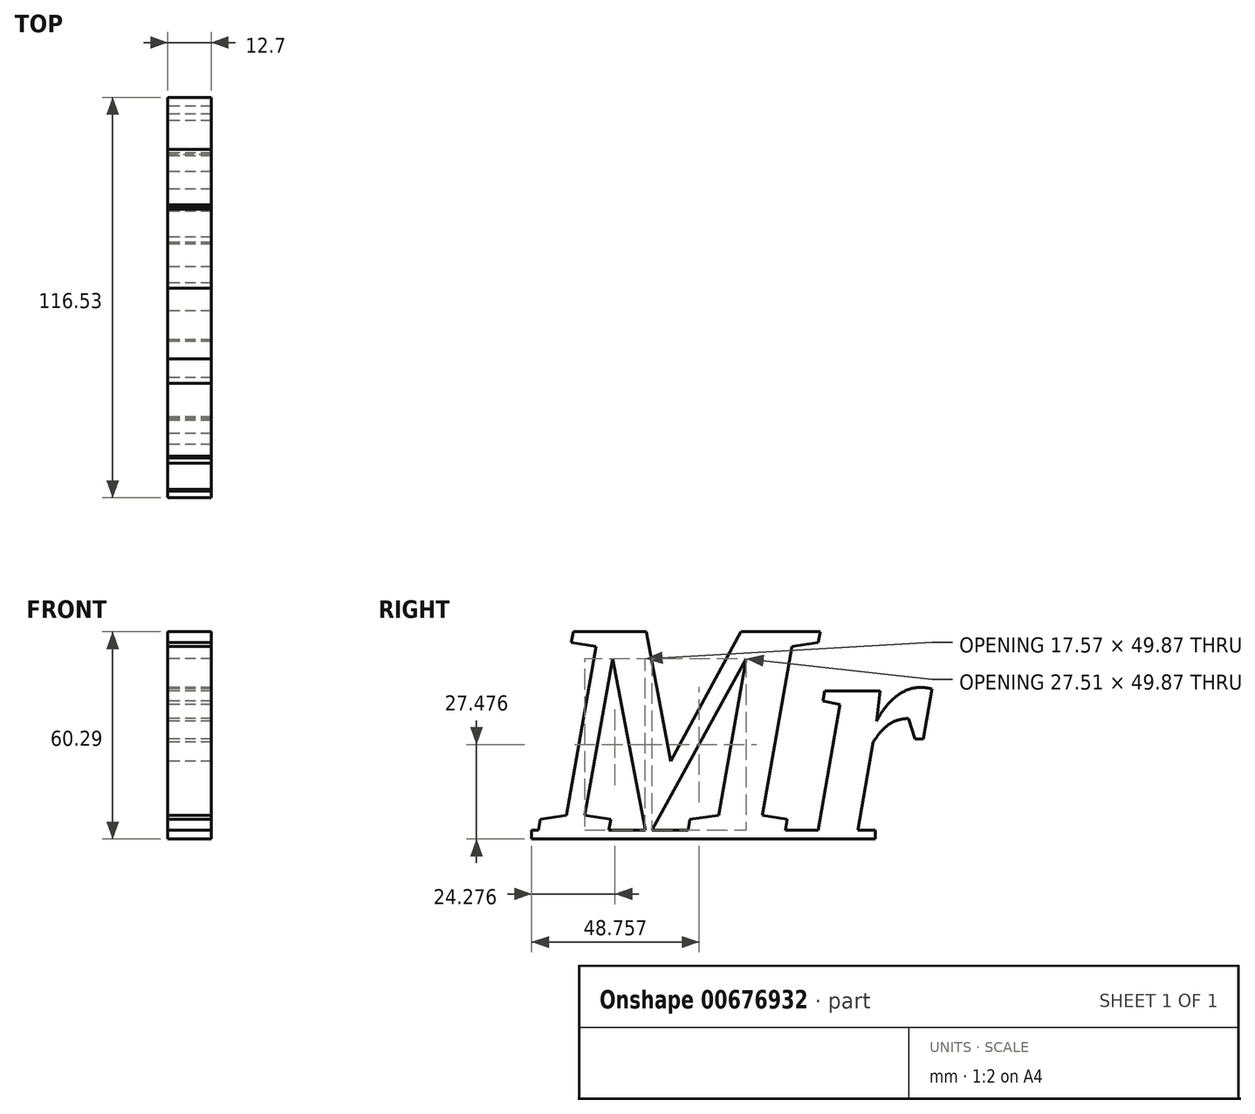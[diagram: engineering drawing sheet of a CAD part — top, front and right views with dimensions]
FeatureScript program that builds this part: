
annotation { "Feature Type Name" : "Feature", "Feature Type Description" : "" }
export const myFeature = defineFeature(function(context is Context, id is Id, definition is map)
    precondition{}
    {
        {
            var Q0;
            Q0=qCreatedBy(makeId("Right.planeOp"),FACE);
            var sketch = newSketch(context, id + "F0", { "sketchPlane" : qUnion([Q0])});
            skLineSegment(sketch, "E0.bottom", {"start": v(19.6, -2.54) * mm, "end": v(-80.4, -2.54) * mm});
            skLineSegment(sketch, "E0.top", {"start": v(19.6, 0) * mm, "end": v(-80.4, 0) * mm});
            skLineSegment(sketch, "E0.left", {"start": v(19.6, -2.54) * mm, "end": v(19.6, 0) * mm});
            skLineSegment(sketch, "E0.right", {"start": v(-80.4, -2.54) * mm, "end": v(-80.4, 0) * mm});
            skSolve(sketch);
        }
        {
            var Q0;
            Q0=qSketchRegion(id+"F0",true);
            extrude(context, id + "F1", {"entities" : qUnion([Q0]), "endBound" : BoundingType.SYMMETRIC, "oppositeDirection" : true, "depth" : 12.7 * mm, "offsetDistance" : 25.4 * mm});
        }
        {
            var Q0;
            Q0=qCreatedBy(makeId("Right.planeOp"),FACE);
            var sketch = newSketch(context, id + "F2", { "sketchPlane" : qUnion([Q0])});
            skText(sketch, "E1", { "text": "Mr", "fontName": "Tinos-BoldItalic.ttf"});
            const initialGuessF2  = {"E1": [-0.07726, 0, 1, 0, 0.0635]};
            skSetInitialGuess(sketch, initialGuessF2);
            skSolve(sketch);
        }
        {
            var Q0;
            Q0=qSketchRegion(id+"F2",true);
            extrude(context, id + "F3", {"entities" : qUnion([Q0]), "operationType" : NewBodyOperationType.ADD, "endBound" : BoundingType.SYMMETRIC, "depth" : 12.7 * mm, "offsetDistance" : 25.4 * mm});
        }
    });
